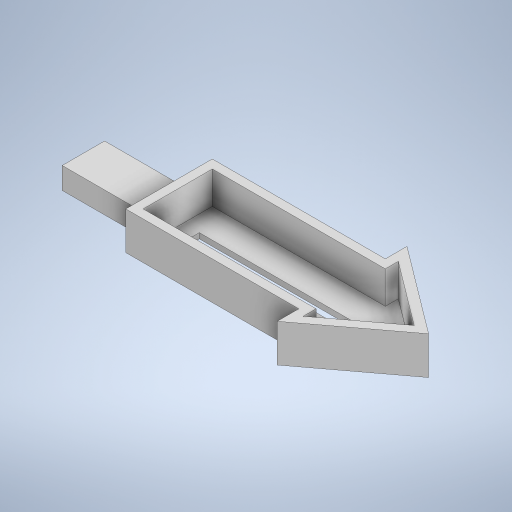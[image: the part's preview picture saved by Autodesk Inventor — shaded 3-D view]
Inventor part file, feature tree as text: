
AUTODESK INVENTOR PART (.ipt)
format: ipt  version: 2023 (Build 270158000, 158)  size: 311,808 bytes
history: native  units: in
note: dims shown in document units (in); Inventor stores cm internally (conversion verified against a paired STEP export)
features: extrude x5, sketch x5, projected_geometry x3
ambient origin geometry x8: Origin, YZ Plane, XZ Plane, XY Plane, X Axis, Y Axis, Z Axis, Center Point
bodies: Solid1 (feature_tree)
feature tree (13):
  extrude  "Extrusion1"  Depth=0.99in
  extrude  "Extrusion2"  Depth=0.495in
  extrude  "Extrusion3"  Depth=1.0in
  extrude  "Extrusion4"  Depth=0.0625in
  extrude  "Extrusion5"  Depth=0.375in
  sketch  "Sketch1"  dims[d0=0.49in d1=0.99in]
  sketch  "Sketch2"  dims[d2=0.245in d3=0.495in]
  projected_geometry  "Projected Loop1"
  sketch  "Sketch3"  dims[d4=0.25in d5=0.0in d6=1.0in]
  projected_geometry  "Projected Loop2"
  sketch  "Sketch4"  dims[d7=0.5in d8=0.0625in]
  projected_geometry  "Projected Loop3"
  sketch  "Sketch6"  dims[d9=2.0in d10=0.0in d11=1.5in d12=0.25in d13=0.5in d14=0.5in d15=1.0in d16=2.0in d17=2.0in d18=0.0625in d19=0.0in d20=0.1in d21=0.375in d22=0.0in d23=0.125in d24=0.0625in d25=0.375in d26=0.0in]
